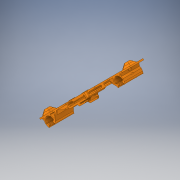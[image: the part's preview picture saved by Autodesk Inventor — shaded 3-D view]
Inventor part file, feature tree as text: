
AUTODESK INVENTOR PART (.ipt)
format: ipt  version: 2017 (Build 210142000, 142)  size: 1,227,776 bytes
history: native  units: in
note: dims shown in document units (in); Inventor stores cm internally (conversion verified against a paired STEP export)
features: extrude x3, sketch x3, other x2, projected_geometry x2, plane x1
ambient origin geometry x8: Origin, YZ Plane, XZ Plane, XY Plane, X Axis, Y Axis, Z Axis, Center Point
bodies: Solid1 (feature_tree)
feature tree (11):
  other  "10_Support plateau.STEP"
  plane  "Work Plane1"
  extrude  "Extrusion1"  Depth=0.3937in TaperAngle=0.0deg
  extrude  "Extrusion2"  Depth=0.3937in TaperAngle=0.0deg
  extrude  "Extrusion3"  [1 undecoded]
  sketch  "Sketch1"  dims[d0=0.0in d1=0.3937in d2=0.0in]
  projected_geometry  "Projected Loop1"
  projected_geometry  "Projected Loop2"
  sketch  "Sketch3"  dims[d3=0.3937in d4=0.0in d5=0.3937in d6=0.0in]
  sketch  "Sketch5"
  parser-record x1  (decoder bookkeeping rows leaked as tree rows — omitted from the tree; the rows remain in map.json)
note: 1 required parameter value undecoded (feature->parameter linkage not recoverable at this tier; creation-order binding heuristic only, values carry confidence <= 0.55)
